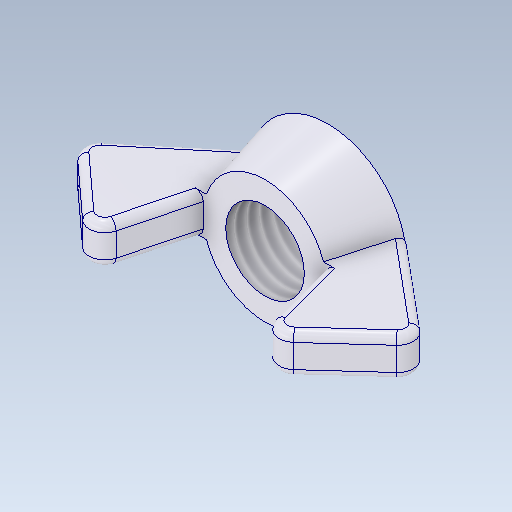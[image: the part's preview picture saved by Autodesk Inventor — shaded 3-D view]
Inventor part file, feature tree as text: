
AUTODESK INVENTOR PART (.ipt)
format: ipt  version: 2020 (Build 240168000, 168)  size: 199,680 bytes
history: native  units: mm
features: sketch x2, other x1, revolve x1, extrude x1, fillet x1, thread x1
ambient origin geometry x8: Origin, YZ Plane, XZ Plane, XY Plane, X Axis, Y Axis, Z Axis, Center Point
bodies: Body1 (feature_tree)
feature tree (7):
  other  "Твердое тело1"
  revolve  "Вращение1"
  extrude  "Выдавливание1"  TaperAngle=90.0deg  [1 undecoded]
  fillet  "Сопряжение1"  Radius=2.5mm
  thread  "Резьба1"
  sketch  "Эскиз1"
  sketch  "Эскиз2"
note: 1 required parameter value undecoded (feature->parameter linkage not recoverable at this tier; creation-order binding heuristic only, values carry confidence <= 0.55)
